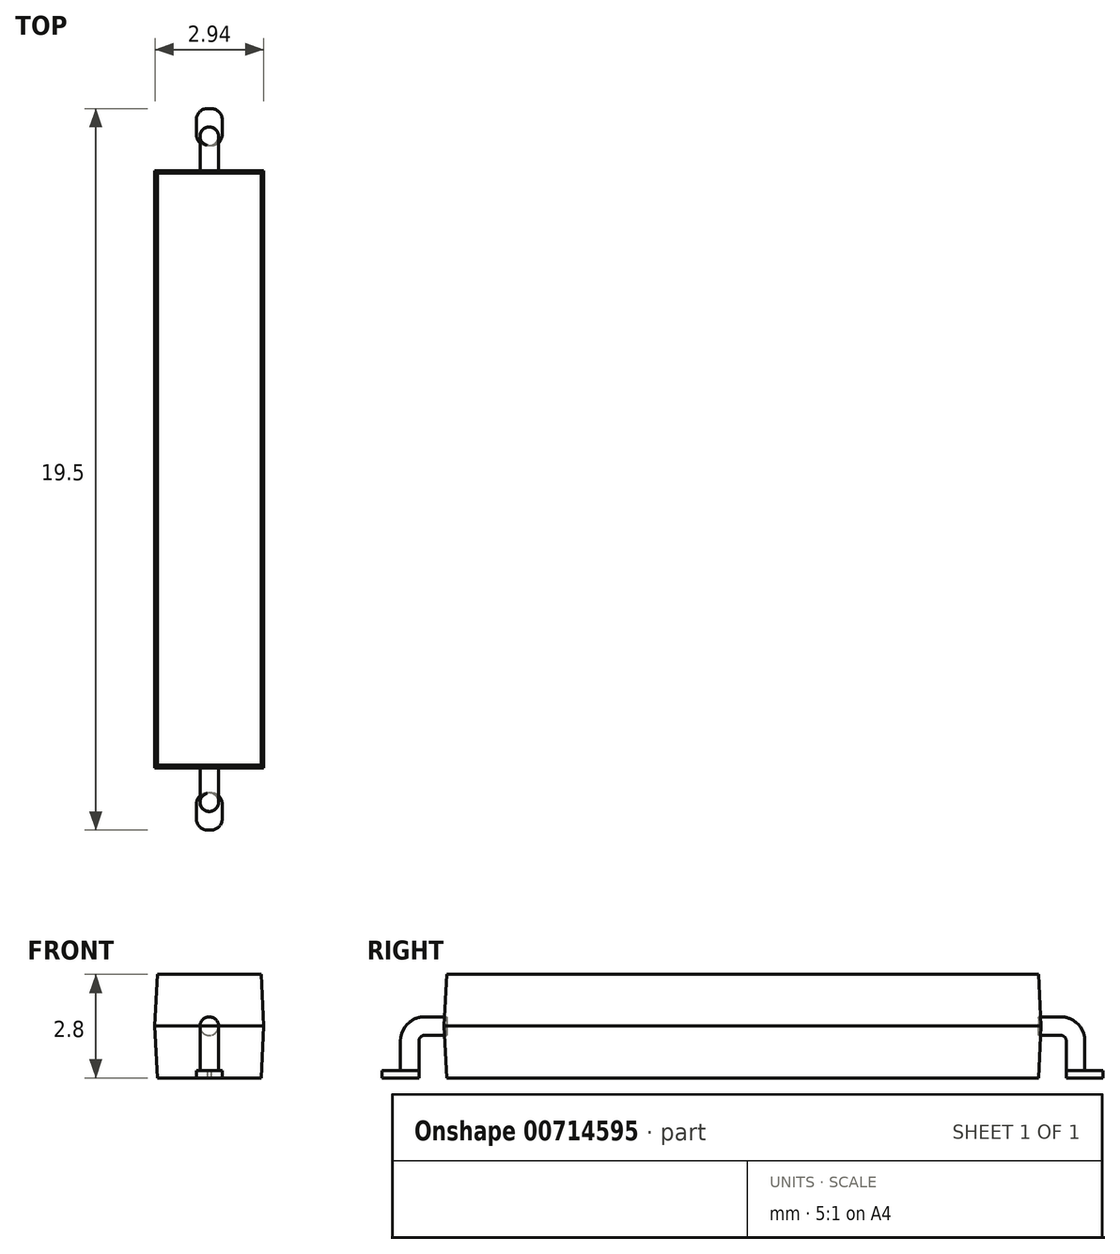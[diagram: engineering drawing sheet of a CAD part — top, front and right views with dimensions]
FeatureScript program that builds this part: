
annotation { "Feature Type Name" : "Feature", "Feature Type Description" : "" }
export const myFeature = defineFeature(function(context is Context, id is Id, definition is map)
    precondition{}
    {
        {
            var Q0;
            Q0=qCreatedBy(makeId("Top.planeOp"),FACE);
            var sketch = newSketch(context, id + "F0", { "sketchPlane" : qUnion([Q0])});
            skLineSegment(sketch, "E0.bottom", {"start": v(1.4, 8) * mm, "end": v(-1.4, 8) * mm});
            skLineSegment(sketch, "E0.top", {"start": v(1.4, -8) * mm, "end": v(-1.4, -8) * mm});
            skLineSegment(sketch, "E0.left", {"start": v(1.4, 8) * mm, "end": v(1.4, -8) * mm});
            skLineSegment(sketch, "E0.right", {"start": v(-1.4, 8) * mm, "end": v(-1.4, -8) * mm});
            skPoint(sketch, "E0.middle", {"position": v(0, 0) * mm});
            skSolve(sketch);
        }
        {
            var Q0;
            Q0=qSketchRegion(id+"F0",true);
            extrude(context, id + "F1", {"entities" : qUnion([Q0]), "depth" : 1.4 * mm, "hasDraft" : true, "draftAngle" : 3 * degree});
        }
        {
            var Q0;
            Q0=makeQuery(id+"F1.opExtrude","CAP_FACE",FACE,{"disambiguationData":[OSD([sQuery(id+"F0.wireOp",EDGE,"E0.bottom"),sQuery(id+"F0.wireOp",EDGE,"E0.top"),sQuery(id+"F0.wireOp",EDGE,"E0.left"),sQuery(id+"F0.wireOp",EDGE,"E0.right")])],"isStart":false});
            extrude(context, id + "F2", {"entities" : qUnion([Q0]), "operationType" : NewBodyOperationType.ADD, "depth" : 1.4 * mm, "hasDraft" : true, "draftAngle" : 3 * degree, "draftPullDirection" : true});
        }
        {
            var Q0;
            Q0=qCreatedBy(makeId("Top.planeOp"),FACE);
            var sketch = newSketch(context, id + "F3", { "sketchPlane" : qUnion([Q0])});
            skLineSegment(sketch, "E1.bottom", {"start": v(0.05, -8.75) * mm, "end": v(-0.05, -8.75) * mm});
            skLineSegment(sketch, "E1.top", {"start": v(0.05, -9.75) * mm, "end": v(-0.05, -9.75) * mm});
            skLineSegment(sketch, "E1.left", {"start": v(0.35, -9.05) * mm, "end": v(0.35, -9.45) * mm});
            skLineSegment(sketch, "E1.right", {"start": v(-0.35, -9.05) * mm, "end": v(-0.35, -9.45) * mm});
            skPoint(sketch, "E1.middle", {"position": v(0, -9.25) * mm});
            skPoint(sketch, "E2.visualSharp", {"position": v(-0.35, -8.75) * mm});
            skArc(sketch, "E2.filletArc", {"start": v(-0.05, -8.75) * mm, "mid": v(-0.26, -8.84) * mm, "end": v(-0.35, -9.05) * mm});
            skPoint(sketch, "E3.visualSharp", {"position": v(0.35, -8.75) * mm});
            skArc(sketch, "E3.filletArc", {"start": v(0.35, -9.05) * mm, "mid": v(0.26, -8.84) * mm, "end": v(0.05, -8.75) * mm});
            skPoint(sketch, "E4.visualSharp", {"position": v(0.35, -9.75) * mm});
            skArc(sketch, "E4.filletArc", {"start": v(0.05, -9.75) * mm, "mid": v(0.26, -9.66) * mm, "end": v(0.35, -9.45) * mm});
            skPoint(sketch, "E5.visualSharp", {"position": v(-0.35, -9.75) * mm});
            skArc(sketch, "E5.filletArc", {"start": v(-0.35, -9.45) * mm, "mid": v(-0.26, -9.66) * mm, "end": v(-0.05, -9.75) * mm});
            skSolve(sketch);
        }
        {
            var Q0;
            Q0=qCreatedBy(makeId("Right.planeOp"),FACE);
            var sketch = newSketch(context, id + "F4", { "sketchPlane" : qUnion([Q0])});
            skLineSegment(sketch, "E6", {"start": v(-8, 1.4) * mm, "end": v(-8.6, 1.4) * mm});
            skLineSegment(sketch, "E7", {"start": v(-9, 1) * mm, "end": v(-9, 0) * mm});
            skLineSegment(sketch, "E8", {"start": v(-8, 2.8) * mm, "end": v(-8, 0) * mm, "construction": true});
            skPoint(sketch, "E9.visualSharp", {"position": v(-9, 1.4) * mm});
            skArc(sketch, "E9.filletArc", {"start": v(-8.6, 1.4) * mm, "mid": v(-8.88, 1.28) * mm, "end": v(-9, 1) * mm});
            skSolve(sketch);
        }
        {
            var Q0;
            Q0=qCreatedBy(makeId("Top.planeOp"),FACE);
            var sketch = newSketch(context, id + "F5", { "sketchPlane" : qUnion([Q0])});
            skCircle(sketch, "E10", {"center": v(0, -9) * mm, "radius": 0.25 * mm});
            skSolve(sketch);
        }
        {
            var Q0;
            Q0=makeQuery(id+"F5.imprint","IMPRINT",FACE,{"disambiguationData":[TD([[makeQuery(id+"F5.imprint","IMPRINT",EDGE,{"derivedFrom":sQuery(id+"F5.wireOp",EDGE,"E10")}),1.0]])]});
            var Q1;
            Q1=sQuery(id+"F4.wireOp",EDGE,"E7");
            var Q2;
            Q2=sQuery(id+"F4.wireOp",EDGE,"E9.filletArc");
            var Q3;
            Q3=sQuery(id+"F4.wireOp",EDGE,"E6");
            sweep(context, id + "F6", {"profiles" : qUnion([Q0]), "path" : qUnion([Q1, Q2, Q3])});
        }
        {
            var Q0;
            Q0=qSketchRegion(id+"F3",true);
            extrude(context, id + "F7", {"entities" : qUnion([Q0]), "operationType" : NewBodyOperationType.ADD, "depth" : .2 * mm});
        }
        {
            var Q0;
            Q0=makeQuery(id+"F6.opSweep","SWEPT_BODY",BODY,{"disambiguationData":[OSD([sQuery(id+"F4.wireOp",EDGE,"E6"),sQuery(id+"F5.wireOp",EDGE,"E10")])]});
            var Q1;
            Q1=qCreatedBy(makeId("Front.planeOp"),FACE);
            mirror(context, id + "F8", {"entities" : qUnion([Q0]), "mirrorPlane" : qUnion([Q1])});
        }
    });
